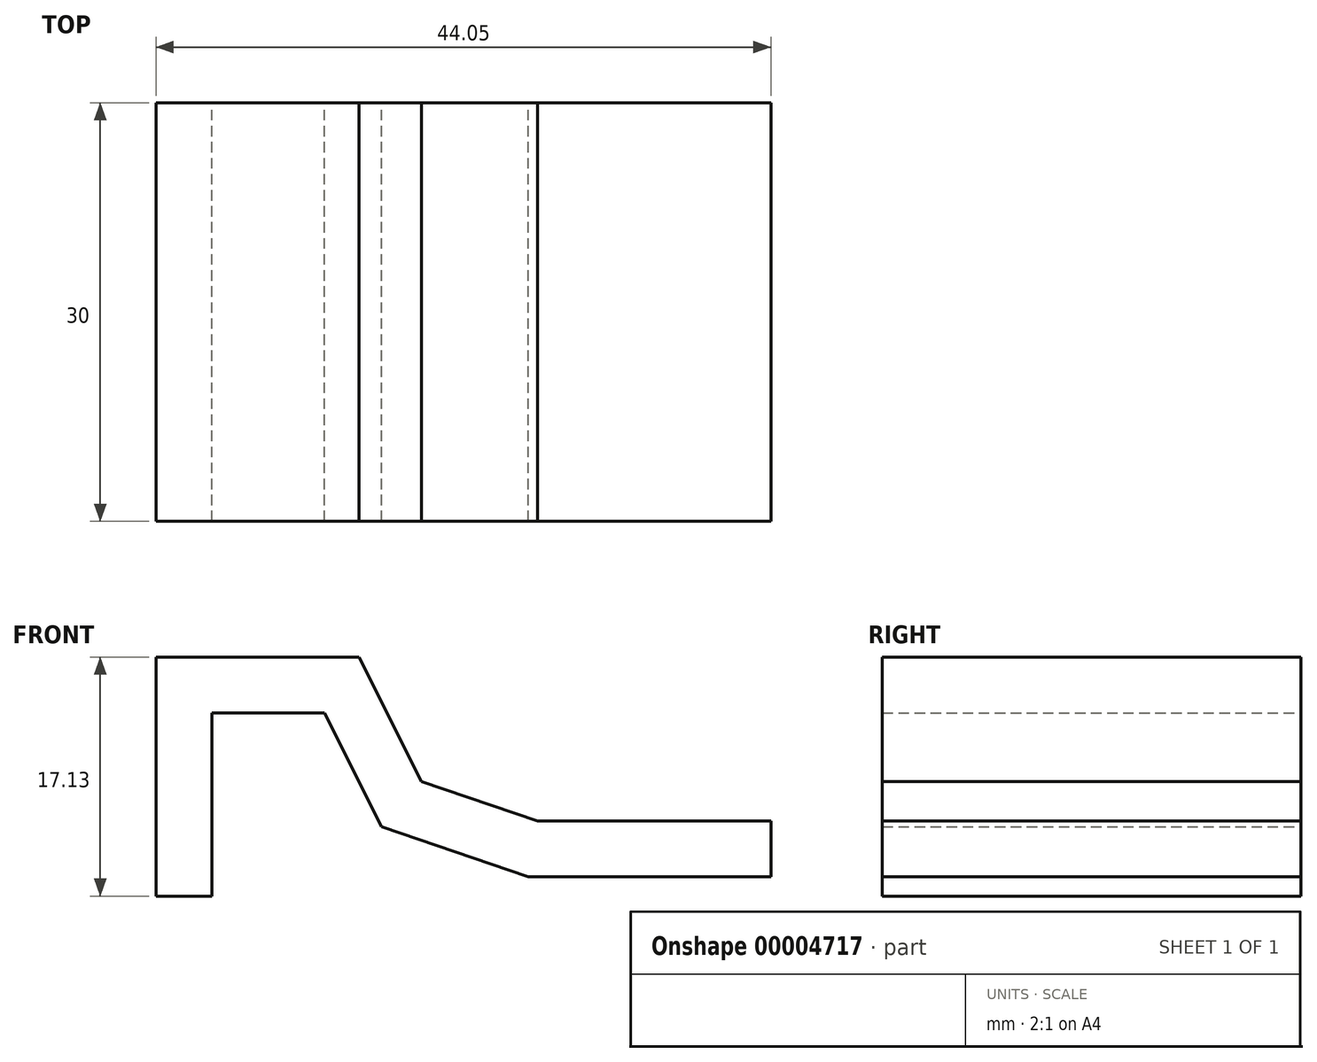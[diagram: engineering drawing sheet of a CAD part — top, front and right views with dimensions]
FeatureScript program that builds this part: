
annotation { "Feature Type Name" : "Feature", "Feature Type Description" : "" }
export const myFeature = defineFeature(function(context is Context, id is Id, definition is map)
    precondition{}
    {
        {
            var Q0;
            Q0=qCreatedBy(makeId("Right.planeOp"),FACE);
            var sketch = newSketch(context, id + "F0", { "sketchPlane" : qUnion([Q0])});
            skLineSegment(sketch, "E0.bottom", {"start": v(-26.43, 9.96) * mm, "end": v(-56.43, 9.96) * mm});
            skLineSegment(sketch, "E0.top", {"start": v(-26.43, 13.96) * mm, "end": v(-56.43, 13.96) * mm});
            skLineSegment(sketch, "E0.left", {"start": v(-26.43, 9.96) * mm, "end": v(-26.43, 13.96) * mm});
            skLineSegment(sketch, "E0.right", {"start": v(-56.43, 9.96) * mm, "end": v(-56.43, 13.96) * mm});
            skSolve(sketch);
        }
        {
            var Q0;
            Q0=qCreatedBy(makeId("Front.planeOp"),FACE);
            var sketch = newSketch(context, id + "F1", { "sketchPlane" : qUnion([Q0])});
            skLineSegment(sketch, "E1", {"start": v(-5.69, 8.39) * mm, "end": v(-17.64, 8.39) * mm});
            skLineSegment(sketch, "E2", {"start": v(-17.64, 8.39) * mm, "end": v(-29.01, 12.24) * mm});
            skLineSegment(sketch, "E3", {"start": v(-29.01, 12.24) * mm, "end": v(-32.95, 20.12) * mm});
            skLineSegment(sketch, "E4", {"start": v(-32.95, 20.12) * mm, "end": v(-38.47, 20.12) * mm});
            skPoint(sketch, "E5.start.orphan", {"position": v(-38.47, 8.39) * mm});
            skLineSegment(sketch, "E6", {"start": v(-38.47, 20.12) * mm, "end": v(-38.47, 2.88) * mm});
            skSolve(sketch);
        }
        {
            var Q0;
            Q0=makeQuery(id+"F0.imprint","IMPRINT",FACE,{"disambiguationData":[TD([[makeQuery(id+"F0.imprint","IMPRINT",EDGE,{"derivedFrom":sQuery(id+"F0.wireOp",EDGE,"E0.bottom")}),-1.0]])]});
            var Q1;
            Q1=sQuery(id+"F1.wireOp",EDGE,"E1");
            var Q2;
            Q2=sQuery(id+"F1.wireOp",EDGE,"E2");
            var Q3;
            Q3=sQuery(id+"F1.wireOp",EDGE,"E3");
            var Q4;
            Q4=sQuery(id+"F1.wireOp",EDGE,"E4");
            var Q5;
            Q5=sQuery(id+"F1.wireOp",EDGE,"E6");
            sweep(context, id + "F2", {"profiles" : qUnion([Q0]), "path" : qUnion([Q1, Q2, Q3, Q4, Q5])});
        }
    });
